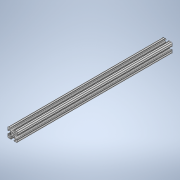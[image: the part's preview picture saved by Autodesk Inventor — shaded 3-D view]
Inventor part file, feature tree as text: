
AUTODESK INVENTOR PART (.ipt)
format: ipt  version: 2020 (Build 240168000, 168)  size: 236,544 bytes
history: native  units: in
note: dims shown in document units (in); Inventor stores cm internally (conversion verified against a paired STEP export)
features: extrude x1, sketch x1
ambient origin geometry x8: Origin, YZ Plane, XZ Plane, XY Plane, X Axis, Y Axis, Z Axis, Center Point
bodies: Solid1 (feature_tree)
feature tree (2):
  extrude  "Extrusion1"  [1 undecoded]
  sketch  "Sketch1"  dims[d0=16.0in d1=0.0in]
note: 1 required parameter value undecoded (feature->parameter linkage not recoverable at this tier; creation-order binding heuristic only, values carry confidence <= 0.55)
